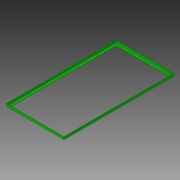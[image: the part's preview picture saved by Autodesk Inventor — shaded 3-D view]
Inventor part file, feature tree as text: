
AUTODESK INVENTOR PART (.ipt)
format: ipt  version: 2019 (Build 230136000, 136)  size: 101,376 bytes
history: native  units: mm
features: extrude x2, sketch x2
ambient origin geometry x8: Origin, YZ Plane, XZ Plane, XY Plane, X Axis, Y Axis, Z Axis, Center Point
bodies: Body1 (feature_tree)
feature tree (4):
  extrude  "Base thickness"  Depth=1105.0mm
  extrude  "Wall height"  Depth=25.4mm
  sketch  "Sketch1"  dims[d0=580.0mm d1=1105.0mm]
  sketch  "Sketch3"  dims[d8=25.4mm d9=25.4mm d12=3.0mm d13=0.0mm d14=3.0mm d15=3.0mm d16=22.4mm d17=0.0mm]
